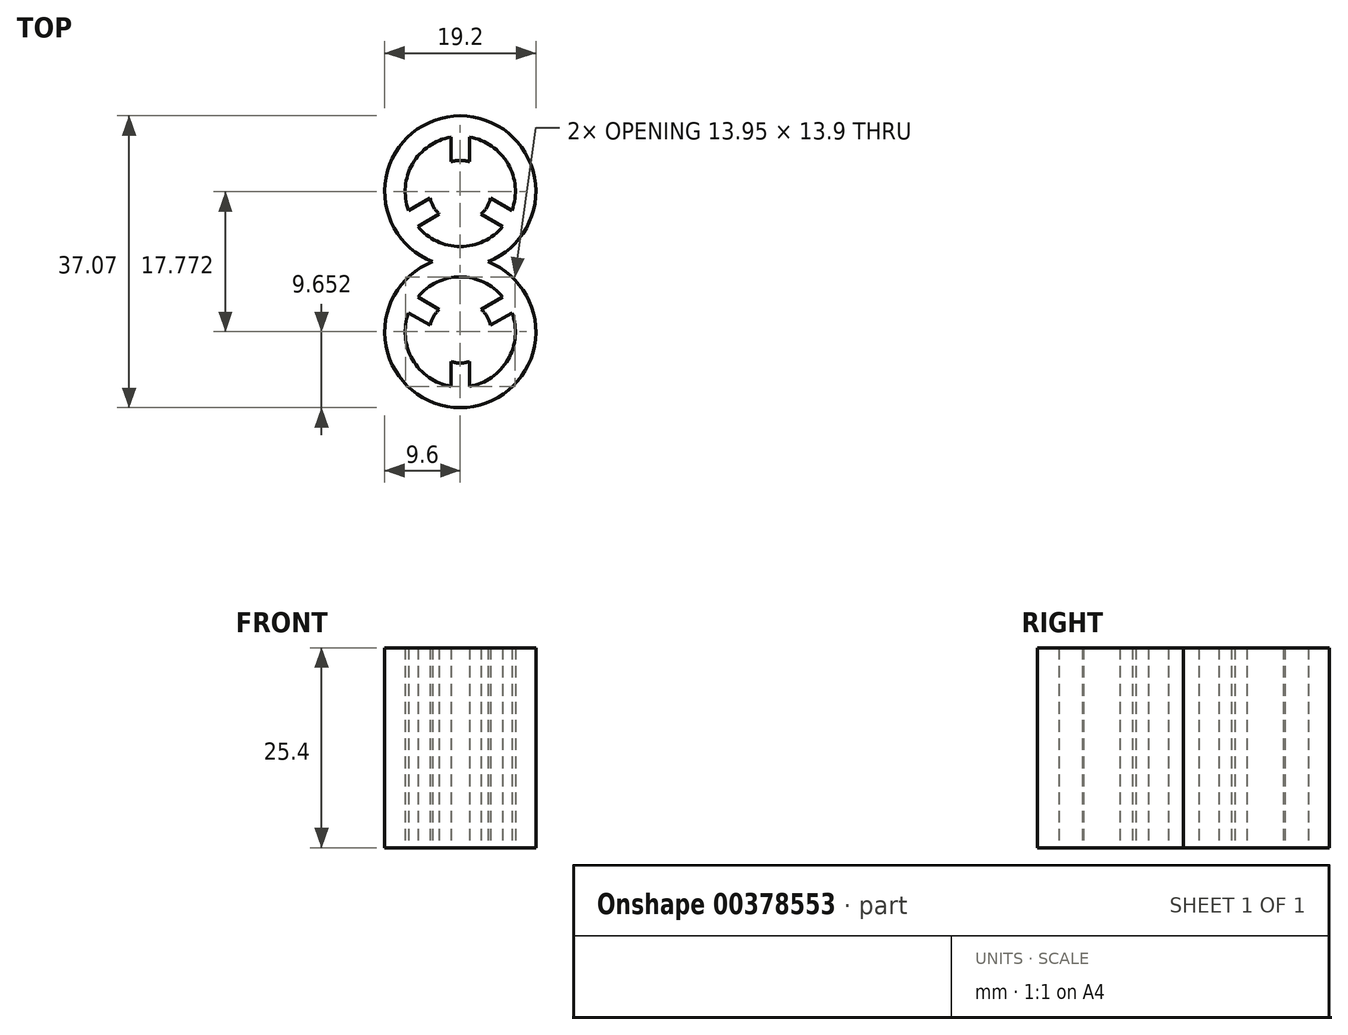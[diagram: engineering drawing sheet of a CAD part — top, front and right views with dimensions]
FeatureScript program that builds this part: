
annotation { "Feature Type Name" : "Feature", "Feature Type Description" : "" }
export const myFeature = defineFeature(function(context is Context, id is Id, definition is map)
    precondition{}
    {
        {
            var Q0;
            Q0=qCreatedBy(makeId("Top.planeOp"),FACE);
            var sketch = newSketch(context, id + "F0", { "sketchPlane" : qUnion([Q0])});
            skArc(sketch, "E0", {"start": v(3.5, 0.76) * mm, "mid": v(0, 19.3) * mm, "end": v(-3.5, 0.76) * mm});
            skArc(sketch, "E1", {"start": v(-1.17, 16.6) * mm, "mid": v(-6.06, 13.2) * mm, "end": v(-6.56, 7.25) * mm});
            skLineSegment(sketch, "E2.left", {"start": v(1.17, 16.6) * mm, "end": v(1.17, 13.45) * mm});
            skLineSegment(sketch, "E2.right", {"start": v(-1.17, 16.6) * mm, "end": v(-1.17, 13.45) * mm});
            skPoint(sketch, "E2.middle", {"position": v(0, 15.02) * mm});
            skArc(sketch, "E3", {"start": v(1.17, 13.45) * mm, "mid": v(0, 13.63) * mm, "end": v(-1.17, 13.45) * mm});
            skLineSegment(sketch, "E4.1.0", {"start": v(-6.56, 7.25) * mm, "end": v(-3.84, 8.83) * mm});
            skArc(sketch, "E4.1.1", {"start": v(-3.84, 8.83) * mm, "mid": v(-3.4, 7.73) * mm, "end": v(-2.67, 6.8) * mm});
            skLineSegment(sketch, "E4.1.2", {"start": v(-5.4, 5.23) * mm, "end": v(-2.67, 6.8) * mm});
            skPoint(sketch, "E4.1.3", {"position": v(-4.62, 7.03) * mm});
            skLineSegment(sketch, "E4.2.0", {"start": v(5.4, 5.23) * mm, "end": v(2.67, 6.8) * mm});
            skArc(sketch, "E4.2.1", {"start": v(2.67, 6.8) * mm, "mid": v(3.4, 7.73) * mm, "end": v(3.84, 8.83) * mm});
            skLineSegment(sketch, "E4.2.2", {"start": v(6.56, 7.25) * mm, "end": v(3.84, 8.83) * mm});
            skPoint(sketch, "E4.2.3", {"position": v(4.62, 7.03) * mm});
            skArc(sketch, "E5.trimOffspring", {"start": v(-5.4, 5.23) * mm, "mid": v(0, 2.7) * mm, "end": v(5.4, 5.23) * mm});
            skArc(sketch, "E6.trimOffspring", {"start": v(6.56, 7.25) * mm, "mid": v(6.06, 13.2) * mm, "end": v(1.17, 16.6) * mm});
            skLineSegment(sketch, "E7", {"start": v(-13.43, 0.76) * mm, "end": v(16.05, 0.76) * mm, "construction": true});
            skArc(sketch, "E8.MirrorCS", {"start": v(-5.4, -3.71) * mm, "mid": v(0, -1.18) * mm, "end": v(5.4, -3.71) * mm});
            skPoint(sketch, "E9.MirrorP", {"position": v(4.62, -5.51) * mm});
            skLineSegment(sketch, "E10.MirrorCS", {"start": v(-5.4, -3.71) * mm, "end": v(-2.67, -5.29) * mm});
            skArc(sketch, "E11.MirrorCS", {"start": v(6.56, -5.74) * mm, "mid": v(6.06, -11.68) * mm, "end": v(1.17, -15.08) * mm});
            skLineSegment(sketch, "E12.MirrorCS", {"start": v(5.4, -3.71) * mm, "end": v(2.67, -5.29) * mm});
            skPoint(sketch, "E13.MirrorP", {"position": v(0, -13.5) * mm});
            skPoint(sketch, "E14.MirrorP", {"position": v(-4.62, -5.51) * mm});
            skArc(sketch, "E15.MirrorCS", {"start": v(-1.17, -15.08) * mm, "mid": v(-6.06, -11.68) * mm, "end": v(-6.56, -5.74) * mm});
            skArc(sketch, "E16.MirrorCS", {"start": v(-3.84, -7.3) * mm, "mid": v(-3.4, -6.2) * mm, "end": v(-2.67, -5.29) * mm});
            skLineSegment(sketch, "E17.MirrorCS", {"start": v(6.56, -5.74) * mm, "end": v(3.84, -7.3) * mm});
            skLineSegment(sketch, "E18.MirrorCS", {"start": v(-1.17, -15.08) * mm, "end": v(-1.17, -11.93) * mm});
            skLineSegment(sketch, "E19.MirrorCS", {"start": v(1.17, -15.08) * mm, "end": v(1.17, -11.93) * mm});
            skArc(sketch, "E20.MirrorC", {"start": v(3.5, 0.76) * mm, "mid": v(0, -17.78) * mm, "end": v(-3.5, 0.76) * mm});
            skArc(sketch, "E21.MirrorCS", {"start": v(2.67, -5.29) * mm, "mid": v(3.4, -6.2) * mm, "end": v(3.84, -7.3) * mm});
            skArc(sketch, "E22.MirrorCS", {"start": v(1.17, -11.93) * mm, "mid": v(0, -12.11) * mm, "end": v(-1.17, -11.93) * mm});
            skLineSegment(sketch, "E23.MirrorCS", {"start": v(-6.56, -5.74) * mm, "end": v(-3.84, -7.3) * mm});
            skSolve(sketch);
        }
        {
            var Q0;
            Q0 = qSketchRegion(id + "F0", true);
            extrude(context, id + "F1", {"entities" : qUnion([Q0]), "depth" : 25.4 * mm});
        }
    });
